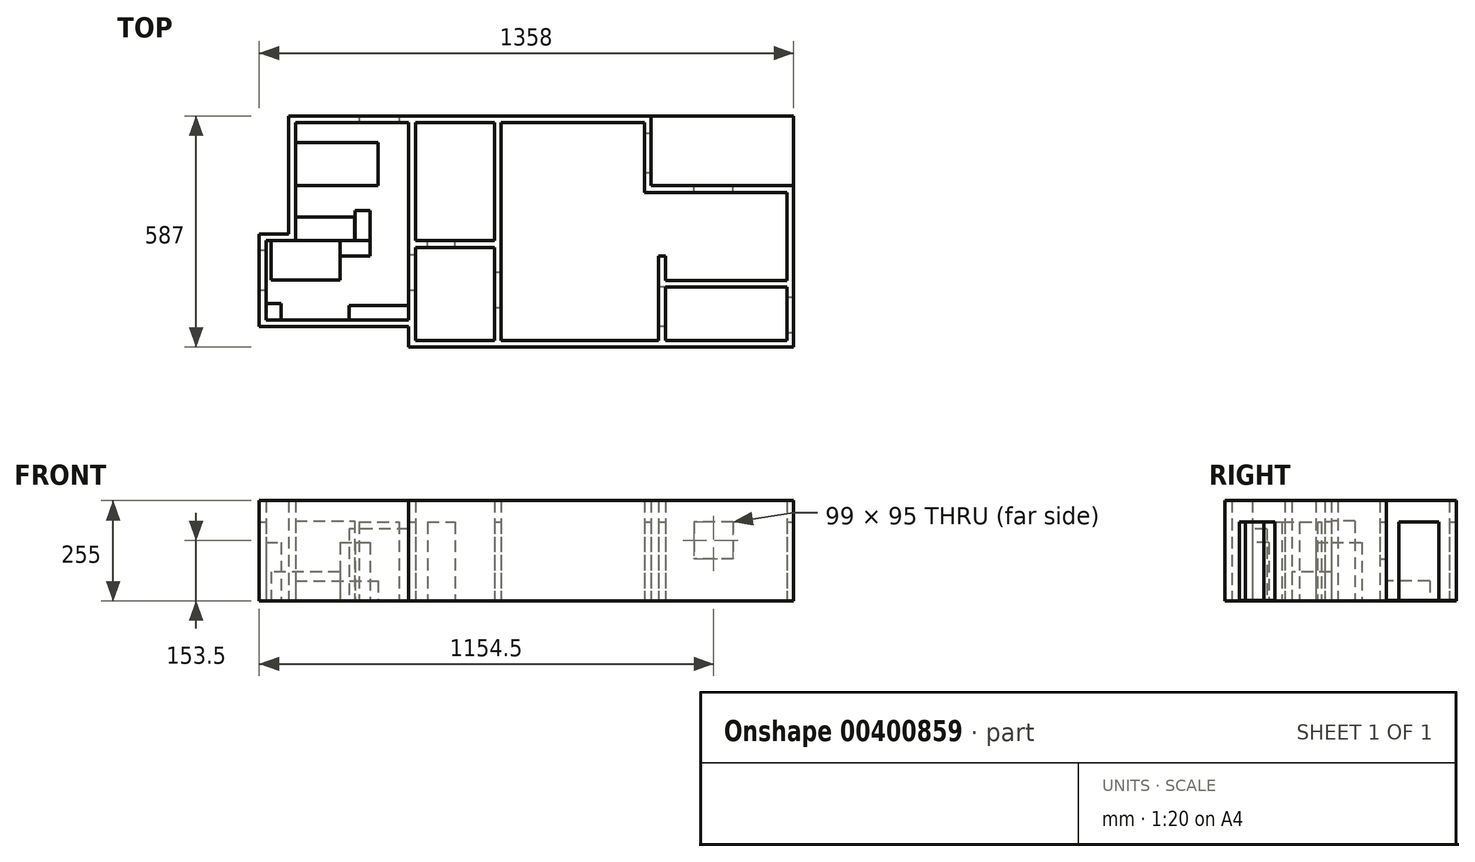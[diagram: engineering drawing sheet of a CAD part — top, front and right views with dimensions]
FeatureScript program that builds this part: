
annotation { "Feature Type Name" : "Feature", "Feature Type Description" : "" }
export const myFeature = defineFeature(function(context is Context, id is Id, definition is map)
    precondition{}
    {
        {
            var Q0;
            Q0=qCreatedBy(makeId("Top.planeOp"),FACE);
            var sketch = newSketch(context, id + "F0", { "sketchPlane" : qUnion([Q0])});
            skLineSegment(sketch, "E0", {"start": v(0, 0) * mm, "end": v(0, 235) * mm});
            skLineSegment(sketch, "E1", {"start": v(0, 235) * mm, "end": v(75, 235) * mm});
            skLineSegment(sketch, "E2", {"start": v(75, 235) * mm, "end": v(75, 535) * mm});
            skLineSegment(sketch, "E3", {"start": v(75, 535) * mm, "end": v(996, 535) * mm});
            skLineSegment(sketch, "E4", {"start": v(0, 0) * mm, "end": v(380, 0) * mm});
            skLineSegment(sketch, "E5.1", {"start": v(92, 518) * mm, "end": v(380, 518) * mm});
            skLineSegment(sketch, "E5.2", {"start": v(92, 218) * mm, "end": v(92, 518) * mm});
            skLineSegment(sketch, "E5.3", {"start": v(380, 17) * mm, "end": v(380, 518) * mm});
            skLineSegment(sketch, "E5.4", {"start": v(17, 17) * mm, "end": v(380, 17) * mm});
            skLineSegment(sketch, "E5.5", {"start": v(17, 17) * mm, "end": v(17, 218) * mm});
            skLineSegment(sketch, "E5.6", {"start": v(17, 218) * mm, "end": v(92, 218) * mm});
            skLineSegment(sketch, "E6", {"start": v(996, 535) * mm, "end": v(996, 358) * mm});
            skLineSegment(sketch, "E7", {"start": v(996, 358) * mm, "end": v(1358, 358) * mm});
            skLineSegment(sketch, "E8", {"start": v(1358, 358) * mm, "end": v(1358, -52) * mm});
            skLineSegment(sketch, "E9", {"start": v(1358, -52) * mm, "end": v(380, -52) * mm});
            skLineSegment(sketch, "E10", {"start": v(380, 0) * mm, "end": v(380, -52) * mm});
            skLineSegment(sketch, "E11.0", {"start": v(397, 201) * mm, "end": v(397, -35) * mm});
            skLineSegment(sketch, "E11.1", {"start": v(1341, -35) * mm, "end": v(1032, -35) * mm});
            skLineSegment(sketch, "E11.2", {"start": v(397, 518) * mm, "end": v(598, 518) * mm});
            skLineSegment(sketch, "E11.3", {"start": v(979, 518) * mm, "end": v(979, 341) * mm});
            skLineSegment(sketch, "E11.4", {"start": v(979, 341) * mm, "end": v(1341, 341) * mm});
            skLineSegment(sketch, "E11.5", {"start": v(1341, 341) * mm, "end": v(1341, 117) * mm});
            skLineSegment(sketch, "E12", {"start": v(397, 218) * mm, "end": v(598, 218) * mm});
            skLineSegment(sketch, "E13", {"start": v(598, 218) * mm, "end": v(598, 518) * mm});
            skLineSegment(sketch, "E14", {"start": v(397, 201) * mm, "end": v(598, 201) * mm});
            skLineSegment(sketch, "E15", {"start": v(615, -35) * mm, "end": v(615, 518) * mm});
            skLineSegment(sketch, "E16", {"start": v(598, 201) * mm, "end": v(598, -35) * mm});
            skLineSegment(sketch, "E17", {"start": v(1015, -35) * mm, "end": v(1015, 179) * mm});
            skLineSegment(sketch, "E18", {"start": v(1015, 179) * mm, "end": v(1032, 179) * mm});
            skLineSegment(sketch, "E19", {"start": v(1032, 179) * mm, "end": v(1032, 117) * mm});
            skLineSegment(sketch, "E20", {"start": v(1032, 117) * mm, "end": v(1341, 117) * mm});
            skLineSegment(sketch, "E21", {"start": v(1032, -35) * mm, "end": v(1032, 100) * mm});
            skLineSegment(sketch, "E22", {"start": v(1032, 100) * mm, "end": v(1341, 100) * mm});
            skLineSegment(sketch, "E23.trimOffspring", {"start": v(615, 518) * mm, "end": v(979, 518) * mm});
            skLineSegment(sketch, "E24.trimOffspring", {"start": v(598, -35) * mm, "end": v(397, -35) * mm});
            skLineSegment(sketch, "E25.trimOffspring", {"start": v(1015, -35) * mm, "end": v(615, -35) * mm});
            skLineSegment(sketch, "E26.trimOffspring", {"start": v(1341, 100) * mm, "end": v(1341, -35) * mm});
            skLineSegment(sketch, "E27.trimOffspring", {"start": v(397, 218) * mm, "end": v(397, 518) * mm});
            skSolve(sketch);
        }
        {
            var Q0;
            Q0=makeQuery(id+"F0.imprint","IMPRINT",FACE,{"disambiguationData":[TD([[makeQuery(id+"F0.imprint","IMPRINT",EDGE,{"derivedFrom":sQuery(id+"F0.wireOp",EDGE,"E0")}),-1.0]])]});
            extrude(context, id + "F1", {"entities" : qUnion([Q0]), "depth" : 255 * mm});
        }
        {
            var Q0;
            Q0=makeQuery(id+"F1.opExtrude","CAP_FACE",FACE,{"disambiguationData":[OSD([sQuery(id+"F0.wireOp",EDGE,"E0"),sQuery(id+"F0.wireOp",EDGE,"E1"),sQuery(id+"F0.wireOp",EDGE,"E2"),sQuery(id+"F0.wireOp",EDGE,"E3"),sQuery(id+"F0.wireOp",EDGE,"E4"),sQuery(id+"F0.wireOp",EDGE,"IFaWQedp-HsAQ-X35q-DpfR-x1YJtlryUvmA"),sQuery(id+"F0.wireOp",EDGE,"E5.1"),sQuery(id+"F0.wireOp",EDGE,"E5.2"),sQuery(id+"F0.wireOp",EDGE,"E5.3"),sQuery(id+"F0.wireOp",EDGE,"E5.4"),sQuery(id+"F0.wireOp",EDGE,"E5.5"),sQuery(id+"F0.wireOp",EDGE,"E5.6")])],"isStart":true});
            var sketch = newSketch(context, id + "F2", { "sketchPlane" : qUnion([Q0])});
            skLineSegment(sketch, "E28", {"start": v(0, 0) * mm, "end": v(0, 0) * mm});
            skLineSegment(sketch, "E29", {"start": v(0, 0) * mm, "end": v(0, 52) * mm});
            skLineSegment(sketch, "E30", {"start": v(0, 52) * mm, "end": v(1358, 52) * mm});
            skLineSegment(sketch, "E31", {"start": v(1358, 52) * mm, "end": v(1358, -535) * mm});
            skLineSegment(sketch, "E32", {"start": v(1358, -535) * mm, "end": v(75, -535) * mm});
            skLineSegment(sketch, "E33", {"start": v(75, -535) * mm, "end": v(75, -235) * mm});
            skLineSegment(sketch, "E34", {"start": v(75, -235) * mm, "end": v(0, -235) * mm});
            skLineSegment(sketch, "E35", {"start": v(0, -235) * mm, "end": v(0, 0) * mm});
            skLineSegment(sketch, "E36.bottom", {"start": v(117, -535) * mm, "end": v(218, -535) * mm});
            skLineSegment(sketch, "E36.top", {"start": v(117, -518) * mm, "end": v(218, -518) * mm});
            skLineSegment(sketch, "E36.left", {"start": v(117, -535) * mm, "end": v(117, -518) * mm});
            skLineSegment(sketch, "E36.right", {"start": v(218, -535) * mm, "end": v(218, -518) * mm});
            skLineSegment(sketch, "E37.bottom", {"start": v(254, -518) * mm, "end": v(355, -518) * mm});
            skLineSegment(sketch, "E37.top", {"start": v(254, -535) * mm, "end": v(355, -535) * mm});
            skLineSegment(sketch, "E37.left", {"start": v(254, -518) * mm, "end": v(254, -535) * mm});
            skLineSegment(sketch, "E37.right", {"start": v(355, -518) * mm, "end": v(355, -535) * mm});
            skLineSegment(sketch, "E38.bottom", {"start": v(0, -92) * mm, "end": v(17, -92) * mm});
            skLineSegment(sketch, "E38.top", {"start": v(0, -193) * mm, "end": v(17, -193) * mm});
            skLineSegment(sketch, "E38.left", {"start": v(0, -92) * mm, "end": v(0, -193) * mm});
            skLineSegment(sketch, "E38.right", {"start": v(17, -92) * mm, "end": v(17, -193) * mm});
            skLineSegment(sketch, "E39.bottom", {"start": v(380, -92) * mm, "end": v(397, -92) * mm});
            skLineSegment(sketch, "E39.top", {"start": v(380, -182) * mm, "end": v(397, -182) * mm});
            skLineSegment(sketch, "E39.left", {"start": v(380, -92) * mm, "end": v(380, -182) * mm});
            skLineSegment(sketch, "E39.right", {"start": v(397, -92) * mm, "end": v(397, -182) * mm});
            skLineSegment(sketch, "E40.bottom", {"start": v(691, -535) * mm, "end": v(792, -535) * mm});
            skLineSegment(sketch, "E40.top", {"start": v(691, -518) * mm, "end": v(792, -518) * mm});
            skLineSegment(sketch, "E40.left", {"start": v(691, -535) * mm, "end": v(691, -518) * mm});
            skLineSegment(sketch, "E40.right", {"start": v(792, -535) * mm, "end": v(792, -518) * mm});
            skLineSegment(sketch, "E41.bottom", {"start": v(828, -535) * mm, "end": v(929, -535) * mm});
            skLineSegment(sketch, "E41.top", {"start": v(828, -518) * mm, "end": v(929, -518) * mm});
            skLineSegment(sketch, "E41.left", {"start": v(828, -535) * mm, "end": v(828, -518) * mm});
            skLineSegment(sketch, "E41.right", {"start": v(929, -535) * mm, "end": v(929, -518) * mm});
            skLineSegment(sketch, "E42.bottom", {"start": v(441, -535) * mm, "end": v(542, -535) * mm});
            skLineSegment(sketch, "E42.top", {"start": v(441, -518) * mm, "end": v(542, -518) * mm});
            skLineSegment(sketch, "E42.left", {"start": v(441, -535) * mm, "end": v(441, -518) * mm});
            skLineSegment(sketch, "E42.right", {"start": v(542, -535) * mm, "end": v(542, -518) * mm});
            skLineSegment(sketch, "E43.bottom", {"start": v(427.5, -218) * mm, "end": v(497.5, -218) * mm});
            skLineSegment(sketch, "E43.top", {"start": v(427.5, -201) * mm, "end": v(497.5, -201) * mm});
            skLineSegment(sketch, "E43.left", {"start": v(427.5, -218) * mm, "end": v(427.5, -201) * mm});
            skLineSegment(sketch, "E43.right", {"start": v(497.5, -218) * mm, "end": v(497.5, -201) * mm});
            skLineSegment(sketch, "E44.bottom", {"start": v(598, -137) * mm, "end": v(615, -137) * mm});
            skLineSegment(sketch, "E44.top", {"start": v(598, -47) * mm, "end": v(615, -47) * mm});
            skLineSegment(sketch, "E44.left", {"start": v(598, -137) * mm, "end": v(598, -47) * mm});
            skLineSegment(sketch, "E44.right", {"start": v(615, -137) * mm, "end": v(615, -47) * mm});
            skLineSegment(sketch, "E45.bottom", {"start": v(1015, -100) * mm, "end": v(1032, -100) * mm});
            skLineSegment(sketch, "E45.top", {"start": v(1015, 0) * mm, "end": v(1032, 0) * mm});
            skLineSegment(sketch, "E45.left", {"start": v(1015, -100) * mm, "end": v(1015, 0) * mm});
            skLineSegment(sketch, "E45.right", {"start": v(1032, -100) * mm, "end": v(1032, 0) * mm});
            skLineSegment(sketch, "E46.bottom", {"start": v(979, -490.63) * mm, "end": v(996, -490.63) * mm});
            skLineSegment(sketch, "E46.top", {"start": v(979, -389.63) * mm, "end": v(996, -389.63) * mm});
            skLineSegment(sketch, "E46.left", {"start": v(979, -490.63) * mm, "end": v(979, -389.63) * mm});
            skLineSegment(sketch, "E46.right", {"start": v(996, -490.63) * mm, "end": v(996, -389.63) * mm});
            skLineSegment(sketch, "E47.bottom", {"start": v(1341, -74.25) * mm, "end": v(1358, -74.25) * mm});
            skLineSegment(sketch, "E47.top", {"start": v(1341, 15.75) * mm, "end": v(1358, 15.75) * mm});
            skLineSegment(sketch, "E47.left", {"start": v(1341, -74.25) * mm, "end": v(1341, 15.75) * mm});
            skLineSegment(sketch, "E47.right", {"start": v(1358, -74.25) * mm, "end": v(1358, 15.75) * mm});
            skSolve(sketch);
        }
        {
            var Q0;
            Q0=makeQuery(id+"F2.imprint","IMPRINT",FACE,{"disambiguationData":[TD([[makeQuery(id+"F2.imprint","IMPRINT",EDGE,{"derivedFrom":sQuery(id+"F2.wireOp",EDGE,"E36.bottom")}),1.0]])]});
            var Q1;
            Q1=makeQuery(id+"F2.imprint","IMPRINT",FACE,{"disambiguationData":[TD([[makeQuery(id+"F2.imprint","IMPRINT",EDGE,{"derivedFrom":sQuery(id+"F2.wireOp",EDGE,"E37.bottom")}),-1.0]])]});
            var Q2;
            Q2=makeQuery(id+"F2.imprint","IMPRINT",FACE,{"disambiguationData":[TD([[makeQuery(id+"F2.imprint","IMPRINT",EDGE,{"derivedFrom":sQuery(id+"F2.wireOp",EDGE,"E39.bottom")}),-1.0]])]});
            var Q3;
            Q3=makeQuery(id+"F2.imprint","IMPRINT",FACE,{"disambiguationData":[TD([[makeQuery(id+"F2.imprint","IMPRINT",EDGE,{"derivedFrom":sQuery(id+"F2.wireOp",EDGE,"E38.bottom")}),-1.0]])]});
            var Q4;
            Q4=makeQuery(id+"F2.imprint","IMPRINT",FACE,{"disambiguationData":[TD([[makeQuery(id+"F2.imprint","IMPRINT",EDGE,{"derivedFrom":sQuery(id+"F2.wireOp",EDGE,"E42.bottom")}),1.0]])]});
            var Q5;
            Q5=makeQuery(id+"F2.imprint","IMPRINT",FACE,{"disambiguationData":[TD([[makeQuery(id+"F2.imprint","IMPRINT",EDGE,{"derivedFrom":sQuery(id+"F2.wireOp",EDGE,"E40.bottom")}),1.0]])]});
            var Q6;
            Q6=makeQuery(id+"F2.imprint","IMPRINT",FACE,{"disambiguationData":[TD([[makeQuery(id+"F2.imprint","IMPRINT",EDGE,{"derivedFrom":sQuery(id+"F2.wireOp",EDGE,"E41.bottom")}),1.0]])]});
            var Q7;
            Q7=makeQuery(id+"F2.imprint","IMPRINT",FACE,{"disambiguationData":[TD([[makeQuery(id+"F2.imprint","IMPRINT",EDGE,{"derivedFrom":sQuery(id+"F2.wireOp",EDGE,"E43.bottom")}),1.0]])]});
            var Q8;
            Q8=makeQuery(id+"F2.imprint","IMPRINT",FACE,{"disambiguationData":[TD([[makeQuery(id+"F2.imprint","IMPRINT",EDGE,{"derivedFrom":sQuery(id+"F2.wireOp",EDGE,"E44.bottom")}),1.0]])]});
            var Q9;
            Q9=makeQuery(id+"F2.imprint","IMPRINT",FACE,{"disambiguationData":[TD([[makeQuery(id+"F2.imprint","IMPRINT",EDGE,{"derivedFrom":sQuery(id+"F2.wireOp",EDGE,"E45.bottom")}),1.0]])]});
            var Q10;
            Q10=makeQuery(id+"F2.imprint","IMPRINT",FACE,{"disambiguationData":[TD([[makeQuery(id+"F2.imprint","IMPRINT",EDGE,{"derivedFrom":sQuery(id+"F2.wireOp",EDGE,"E46.bottom")}),1.0]])]});
            var Q11;
            Q11=makeQuery(id+"F2.imprint","IMPRINT",FACE,{"disambiguationData":[TD([[makeQuery(id+"F2.imprint","IMPRINT",EDGE,{"derivedFrom":sQuery(id+"F2.wireOp",EDGE,"E47.bottom")}),1.0]])]});
            extrude(context, id + "F3", {"entities" : qUnion([Q0, Q1, Q2, Q3, Q4, Q5, Q6, Q7, Q8, Q9, Q10, Q11]), "operationType" : NewBodyOperationType.REMOVE, "oppositeDirection" : true, "depth" : 200 * mm});
        }
        {
            var Q0;
            {var subQ0=sQuery(id+"F0.wireOp",EDGE,"IFaWQedp-HsAQ-X35q-DpfR-x1YJtlryUvmA");var subQ1=sQuery(id+"F0.wireOp",EDGE,"E4");var subQ2=sQuery(id+"F0.wireOp",EDGE,"E5.3");var subQ3=sQuery(id+"F0.wireOp",EDGE,"E0");var subQ4=sQuery(id+"F0.wireOp",EDGE,"E5.4");var subQ5=sQuery(id+"F0.wireOp",EDGE,"E5.5");Q0=makeQuery(id+"F3.boolean.opBoolean","SPLIT",FACE,{"disambiguationData":[TD([makeQuery(id+"F1.opExtrude","SWEPT_FACE",FACE,{"disambiguationData":[OSD([subQ1])]})])],"derivedFrom":makeQuery(id+"F1.opExtrude","CAP_FACE",FACE,{"disambiguationData":[OSD([subQ3,sQuery(id+"F0.wireOp",EDGE,"E1"),sQuery(id+"F0.wireOp",EDGE,"E2"),sQuery(id+"F0.wireOp",EDGE,"E3"),subQ1,subQ0,sQuery(id+"F0.wireOp",EDGE,"E5.1"),sQuery(id+"F0.wireOp",EDGE,"E5.2"),subQ2,subQ4,subQ5,sQuery(id+"F0.wireOp",EDGE,"E5.6")])],"isStart":true})});}
            var sketch = newSketch(context, id + "F4", { "sketchPlane" : qUnion([Q0])});
            skLineSegment(sketch, "E48", {"start": v(1358, -535) * mm, "end": v(75, -535) * mm});
            skLineSegment(sketch, "E49", {"start": v(1358, -535) * mm, "end": v(1358, 52) * mm});
            skLineSegment(sketch, "E50", {"start": v(75, -535) * mm, "end": v(75, -235) * mm});
            skLineSegment(sketch, "E51", {"start": v(75, -235) * mm, "end": v(0, -235) * mm});
            skLineSegment(sketch, "E52", {"start": v(0, -235) * mm, "end": v(0, 0) * mm});
            skLineSegment(sketch, "E53", {"start": v(0, 0) * mm, "end": v(380, 0) * mm});
            skLineSegment(sketch, "E54", {"start": v(380, 0) * mm, "end": v(380, 52) * mm});
            skLineSegment(sketch, "E55", {"start": v(380, 52) * mm, "end": v(1358, 52) * mm});
            skSolve(sketch);
        }
        {
            var Q0;
            Q0 = qSketchRegion(id + "F4", true);
            extrude(context, id + "F5", {"entities" : qUnion([Q0]), "operationType" : NewBodyOperationType.ADD, "oppositeDirection" : true, "depth" : 1 * mm});
        }
        {
            var Q0;
            Q0=makeQuery(id+"F5.opExtrude","CAP_FACE",FACE,{"disambiguationData":[OSD([sQuery(id+"F4.wireOp",EDGE,"WB7iJUcI-Pn1a-4JZh-fcZq-aHBKsxgmeDfg"),sQuery(id+"F4.wireOp",EDGE,"EiC7A44o-HgZC-mgZ0-LeNN-GIA7PSFpgaOl"),sQuery(id+"F4.wireOp",EDGE,"E48"),sQuery(id+"F4.wireOp",EDGE,"E49"),sQuery(id+"F4.wireOp",EDGE,"wNzbY7fW-Y6dv-rFgA-LDM7-SuEzBiaTQcHj"),sQuery(id+"F4.wireOp",EDGE,"Tt0SW3IV-c8Er-OhKk-rjt7-h9siV44ZHD80")])],"isStart":false});
            var sketch = newSketch(context, id + "F6", { "sketchPlane" : qUnion([Q0])});
            skLineSegment(sketch, "E56.bottom", {"start": v(30.3, 218) * mm, "end": v(205.3, 218) * mm});
            skLineSegment(sketch, "E56.top", {"start": v(30.3, 118) * mm, "end": v(205.3, 118) * mm});
            skLineSegment(sketch, "E56.left", {"start": v(30.3, 218) * mm, "end": v(30.3, 118) * mm});
            skLineSegment(sketch, "E56.right", {"start": v(205.3, 218) * mm, "end": v(205.3, 118) * mm});
            skSolve(sketch);
        }
        {
            var Q0;
            {var subQ5=sQuery(id+"F6.wireOp",EDGE,"E56.top");Q0=makeQuery(id+"F6.imprint","IMPRINT",FACE,{"disambiguationData":[TD([[makeQuery(id+"F6.imprint","IMPRINT",EDGE,{"derivedFrom":subQ5}),1.0]])]});}
            extrude(context, id + "F7", {"entities" : qUnion([Q0]), "depth" : 73 * mm});
        }
        {
            var Q0;
            Q0=makeQuery(id+"F5.opExtrude","CAP_FACE",FACE,{"disambiguationData":[OSD([sQuery(id+"F4.wireOp",EDGE,"WB7iJUcI-Pn1a-4JZh-fcZq-aHBKsxgmeDfg"),sQuery(id+"F4.wireOp",EDGE,"EiC7A44o-HgZC-mgZ0-LeNN-GIA7PSFpgaOl"),sQuery(id+"F4.wireOp",EDGE,"E48"),sQuery(id+"F4.wireOp",EDGE,"E49"),sQuery(id+"F4.wireOp",EDGE,"wNzbY7fW-Y6dv-rFgA-LDM7-SuEzBiaTQcHj"),sQuery(id+"F4.wireOp",EDGE,"Tt0SW3IV-c8Er-OhKk-rjt7-h9siV44ZHD80")])],"isStart":false});
            var sketch = newSketch(context, id + "F8", { "sketchPlane" : qUnion([Q0])});
            skLineSegment(sketch, "E57.bottom", {"start": v(380, 17) * mm, "end": v(228, 17) * mm});
            skLineSegment(sketch, "E57.top", {"start": v(380, 54) * mm, "end": v(228, 54) * mm});
            skLineSegment(sketch, "E57.left", {"start": v(380, 17) * mm, "end": v(380, 54) * mm});
            skLineSegment(sketch, "E57.right", {"start": v(228, 17) * mm, "end": v(228, 54) * mm});
            skSolve(sketch);
        }
        {
            var Q0;
            Q0=makeQuery(id+"F8.imprint","IMPRINT",FACE,{"disambiguationData":[TD([[makeQuery(id+"F8.imprint","IMPRINT",EDGE,{"derivedFrom":sQuery(id+"F8.wireOp",EDGE,"E57.bottom")}),-1.0]])]});
            extrude(context, id + "F9", {"entities" : qUnion([Q0]), "depth" : 182 * mm});
        }
        {
            var Q0;
            Q0=makeQuery(id+"F5.opExtrude","CAP_FACE",FACE,{"disambiguationData":[OSD([sQuery(id+"F4.wireOp",EDGE,"WB7iJUcI-Pn1a-4JZh-fcZq-aHBKsxgmeDfg"),sQuery(id+"F4.wireOp",EDGE,"EiC7A44o-HgZC-mgZ0-LeNN-GIA7PSFpgaOl"),sQuery(id+"F4.wireOp",EDGE,"E48"),sQuery(id+"F4.wireOp",EDGE,"E49"),sQuery(id+"F4.wireOp",EDGE,"wNzbY7fW-Y6dv-rFgA-LDM7-SuEzBiaTQcHj"),sQuery(id+"F4.wireOp",EDGE,"Tt0SW3IV-c8Er-OhKk-rjt7-h9siV44ZHD80")])],"isStart":false});
            var sketch = newSketch(context, id + "F10", { "sketchPlane" : qUnion([Q0])});
            skLineSegment(sketch, "E58.bottom", {"start": v(92, 358) * mm, "end": v(302, 358) * mm});
            skLineSegment(sketch, "E58.top", {"start": v(92, 468) * mm, "end": v(302, 468) * mm});
            skLineSegment(sketch, "E58.left", {"start": v(92, 358) * mm, "end": v(92, 468) * mm});
            skLineSegment(sketch, "E58.right", {"start": v(302, 358) * mm, "end": v(302, 468) * mm});
            skSolve(sketch);
        }
        {
            var Q0;
            Q0=makeQuery(id+"F10.imprint","IMPRINT",FACE,{"disambiguationData":[TD([[makeQuery(id+"F10.imprint","IMPRINT",EDGE,{"derivedFrom":sQuery(id+"F10.wireOp",EDGE,"E58.bottom")}),1.0]])]});
            extrude(context, id + "F11", {"entities" : qUnion([Q0]), "depth" : 50 * mm});
        }
        {
            var Q0;
            Q0=makeQuery(id+"F5.opExtrude","CAP_FACE",FACE,{"disambiguationData":[OSD([sQuery(id+"F4.wireOp",EDGE,"WB7iJUcI-Pn1a-4JZh-fcZq-aHBKsxgmeDfg"),sQuery(id+"F4.wireOp",EDGE,"EiC7A44o-HgZC-mgZ0-LeNN-GIA7PSFpgaOl"),sQuery(id+"F4.wireOp",EDGE,"E48"),sQuery(id+"F4.wireOp",EDGE,"E49"),sQuery(id+"F4.wireOp",EDGE,"wNzbY7fW-Y6dv-rFgA-LDM7-SuEzBiaTQcHj"),sQuery(id+"F4.wireOp",EDGE,"Tt0SW3IV-c8Er-OhKk-rjt7-h9siV44ZHD80")])],"isStart":false});
            var sketch = newSketch(context, id + "F12", { "sketchPlane" : qUnion([Q0])});
            skLineSegment(sketch, "E59.bottom", {"start": v(92, 218) * mm, "end": v(242, 218) * mm});
            skLineSegment(sketch, "E59.top", {"start": v(92, 278) * mm, "end": v(242, 278) * mm});
            skLineSegment(sketch, "E59.left", {"start": v(92, 218) * mm, "end": v(92, 278) * mm});
            skLineSegment(sketch, "E59.right", {"start": v(242, 218) * mm, "end": v(242, 278) * mm});
            skSolve(sketch);
        }
        {
            var Q0;
            Q0=makeQuery(id+"F12.imprint","IMPRINT",FACE,{"disambiguationData":[TD([[makeQuery(id+"F12.imprint","IMPRINT",EDGE,{"derivedFrom":sQuery(id+"F12.wireOp",EDGE,"E59.bottom")}),1.0]])]});
            extrude(context, id + "F13", {"entities" : qUnion([Q0]), "depth" : 202 * mm});
        }
        {
            var Q0;
            Q0=makeQuery(id+"F5.opExtrude","CAP_FACE",FACE,{"disambiguationData":[OSD([sQuery(id+"F4.wireOp",EDGE,"WB7iJUcI-Pn1a-4JZh-fcZq-aHBKsxgmeDfg"),sQuery(id+"F4.wireOp",EDGE,"EiC7A44o-HgZC-mgZ0-LeNN-GIA7PSFpgaOl"),sQuery(id+"F4.wireOp",EDGE,"E48"),sQuery(id+"F4.wireOp",EDGE,"E49"),sQuery(id+"F4.wireOp",EDGE,"wNzbY7fW-Y6dv-rFgA-LDM7-SuEzBiaTQcHj"),sQuery(id+"F4.wireOp",EDGE,"Tt0SW3IV-c8Er-OhKk-rjt7-h9siV44ZHD80")])],"isStart":false});
            var sketch = newSketch(context, id + "F14", { "sketchPlane" : qUnion([Q0])});
            skLineSegment(sketch, "E60.bottom", {"start": v(205.3, 179) * mm, "end": v(282.3, 179) * mm});
            skLineSegment(sketch, "E60.top", {"start": v(205.3, 218) * mm, "end": v(282.3, 218) * mm});
            skLineSegment(sketch, "E60.left", {"start": v(205.3, 179) * mm, "end": v(205.3, 218) * mm});
            skLineSegment(sketch, "E60.right", {"start": v(282.3, 179) * mm, "end": v(282.3, 218) * mm});
            skSolve(sketch);
        }
        {
            var Q0;
            Q0=makeQuery(id+"F14.imprint","IMPRINT",FACE,{"disambiguationData":[TD([[makeQuery(id+"F14.imprint","IMPRINT",EDGE,{"derivedFrom":sQuery(id+"F14.wireOp",EDGE,"E60.bottom")}),1.0]])]});
            extrude(context, id + "F15", {"entities" : qUnion([Q0]), "depth" : 147 * mm});
        }
        {
            var Q0;
            Q0=makeQuery(id+"F5.opExtrude","CAP_FACE",FACE,{"disambiguationData":[OSD([sQuery(id+"F4.wireOp",EDGE,"WB7iJUcI-Pn1a-4JZh-fcZq-aHBKsxgmeDfg"),sQuery(id+"F4.wireOp",EDGE,"EiC7A44o-HgZC-mgZ0-LeNN-GIA7PSFpgaOl"),sQuery(id+"F4.wireOp",EDGE,"E48"),sQuery(id+"F4.wireOp",EDGE,"E49"),sQuery(id+"F4.wireOp",EDGE,"wNzbY7fW-Y6dv-rFgA-LDM7-SuEzBiaTQcHj"),sQuery(id+"F4.wireOp",EDGE,"Tt0SW3IV-c8Er-OhKk-rjt7-h9siV44ZHD80")])],"isStart":false});
            var sketch = newSketch(context, id + "F16", { "sketchPlane" : qUnion([Q0])});
            skLineSegment(sketch, "E61.bottom", {"start": v(243.3, 218) * mm, "end": v(282.3, 218) * mm});
            skLineSegment(sketch, "E61.top", {"start": v(243.3, 295) * mm, "end": v(282.3, 295) * mm});
            skLineSegment(sketch, "E61.left", {"start": v(243.3, 218) * mm, "end": v(243.3, 295) * mm});
            skLineSegment(sketch, "E61.right", {"start": v(282.3, 218) * mm, "end": v(282.3, 295) * mm});
            skSolve(sketch);
        }
        {
            var Q0;
            Q0=makeQuery(id+"F16.imprint","IMPRINT",FACE,{"disambiguationData":[TD([[makeQuery(id+"F16.imprint","IMPRINT",EDGE,{"derivedFrom":sQuery(id+"F16.wireOp",EDGE,"E61.bottom")}),1.0]])]});
            extrude(context, id + "F17", {"entities" : qUnion([Q0]), "depth" : 147 * mm});
        }
        {
            var Q0;
            Q0=makeQuery(id+"F5.opExtrude","CAP_FACE",FACE,{"disambiguationData":[OSD([sQuery(id+"F4.wireOp",EDGE,"WB7iJUcI-Pn1a-4JZh-fcZq-aHBKsxgmeDfg"),sQuery(id+"F4.wireOp",EDGE,"EiC7A44o-HgZC-mgZ0-LeNN-GIA7PSFpgaOl"),sQuery(id+"F4.wireOp",EDGE,"E48"),sQuery(id+"F4.wireOp",EDGE,"E49"),sQuery(id+"F4.wireOp",EDGE,"wNzbY7fW-Y6dv-rFgA-LDM7-SuEzBiaTQcHj"),sQuery(id+"F4.wireOp",EDGE,"Tt0SW3IV-c8Er-OhKk-rjt7-h9siV44ZHD80")])],"isStart":false});
            var sketch = newSketch(context, id + "F18", { "sketchPlane" : qUnion([Q0])});
            skLineSegment(sketch, "E62.bottom", {"start": v(17, 17) * mm, "end": v(56, 17) * mm});
            skLineSegment(sketch, "E62.top", {"start": v(17, 59) * mm, "end": v(56, 59) * mm});
            skLineSegment(sketch, "E62.left", {"start": v(17, 17) * mm, "end": v(17, 59) * mm});
            skLineSegment(sketch, "E62.right", {"start": v(56, 17) * mm, "end": v(56, 59) * mm});
            skSolve(sketch);
        }
        {
            var Q0;
            Q0=makeQuery(id+"F18.imprint","IMPRINT",FACE,{"disambiguationData":[TD([[makeQuery(id+"F18.imprint","IMPRINT",EDGE,{"derivedFrom":sQuery(id+"F18.wireOp",EDGE,"E62.bottom")}),-1.0]])]});
            extrude(context, id + "F19", {"entities" : qUnion([Q0]), "depth" : 147 * mm});
        }
        {
            var Q0;
            Q0=makeQuery(id+"F1.opExtrude","SWEPT_FACE",FACE,{"disambiguationData":[OSD([sQuery(id+"F0.wireOp",EDGE,"E7")])]});
            var sketch = newSketch(context, id + "F20", { "sketchPlane" : qUnion([Q0])});
            skLineSegment(sketch, "E63.bottom", {"start": v(-1204, 201) * mm, "end": v(-1105, 201) * mm});
            skLineSegment(sketch, "E63.top", {"start": v(-1204, 106) * mm, "end": v(-1105, 106) * mm});
            skLineSegment(sketch, "E63.left", {"start": v(-1204, 201) * mm, "end": v(-1204, 106) * mm});
            skLineSegment(sketch, "E63.right", {"start": v(-1105, 201) * mm, "end": v(-1105, 106) * mm});
            skSolve(sketch);
        }
        {
            var Q0;
            Q0=makeQuery(id+"F20.imprint","IMPRINT",FACE,{"disambiguationData":[TD([[makeQuery(id+"F20.imprint","IMPRINT",EDGE,{"derivedFrom":sQuery(id+"F20.wireOp",EDGE,"E63.bottom")}),-1.0]])]});
            extrude(context, id + "F21", {"entities" : qUnion([Q0]), "operationType" : NewBodyOperationType.REMOVE, "oppositeDirection" : true, "depth" : 25 * mm});
        }
    });
